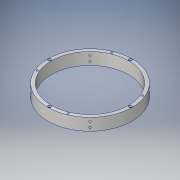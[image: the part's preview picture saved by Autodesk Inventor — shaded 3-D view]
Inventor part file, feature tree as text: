
AUTODESK INVENTOR PART (.ipt)
format: ipt  version: 2016 SP1 (Build 200210100, 210)  size: 181,760 bytes
history: native  units: in
note: dims shown in document units (in); Inventor stores cm internally (conversion verified against a paired STEP export)
features: sketch x5, hole x3, pattern_circular x3, extrude x1, plane x1
ambient origin geometry x8: Origin, YZ Plane, XZ Plane, XY Plane, X Axis, Y Axis, Z Axis, Center Point
bodies: Solid1 (feature_tree)
feature tree (13):
  extrude  "Extrusion1"  Depth=0.5in
  hole  "Hole1"  [1 undecoded]
  pattern_circular  "Circular Pattern1"  Count=4 Angle=360.0deg
  sketch  "Sketch3"  dims[d5=0.266in d6=0.5in d7=0.438in d8=0.25in d9=0.5635in d10=1.0in d11=0.8108in d12=1.5748in d13=360.0deg]
  plane  "Work Plane1"
  hole  "Hole2"  [1 undecoded]
  pattern_circular  "Circular Pattern2"  Count=4 Angle=360.0deg
  hole  "Hole3"  [1 undecoded]
  pattern_circular  "Circular Pattern3"  Angle=22.5deg  [1 undecoded]
  sketch  "Sketch1"  dims[d0=12.25in d1=0.5in]
  sketch  "Sketch2"  dims[d2=1.75in d3=0.0in d4=5.875in]
  sketch  "Sketch4"  dims[d15=135.0deg d16=0.5in]
  sketch  "Sketch5"  dims[d17=0.75in d18=0.257in d19=0.5in d20=0.507in d21=0.25in d22=0.5635in d23=1.0in d24=0.8108in d25=1.5748in d26=360.0deg d28=5.875in d29=22.5deg d30=0.266in d31=0.75in d32=0.507in d33=0.25in d34=0.5635in d35=1.0in d36=0.8108in d37=1.5748in d38=360.0deg]
note: 4 required parameter values undecoded (feature->parameter linkage not recoverable at this tier; creation-order binding heuristic only, values carry confidence <= 0.55)
